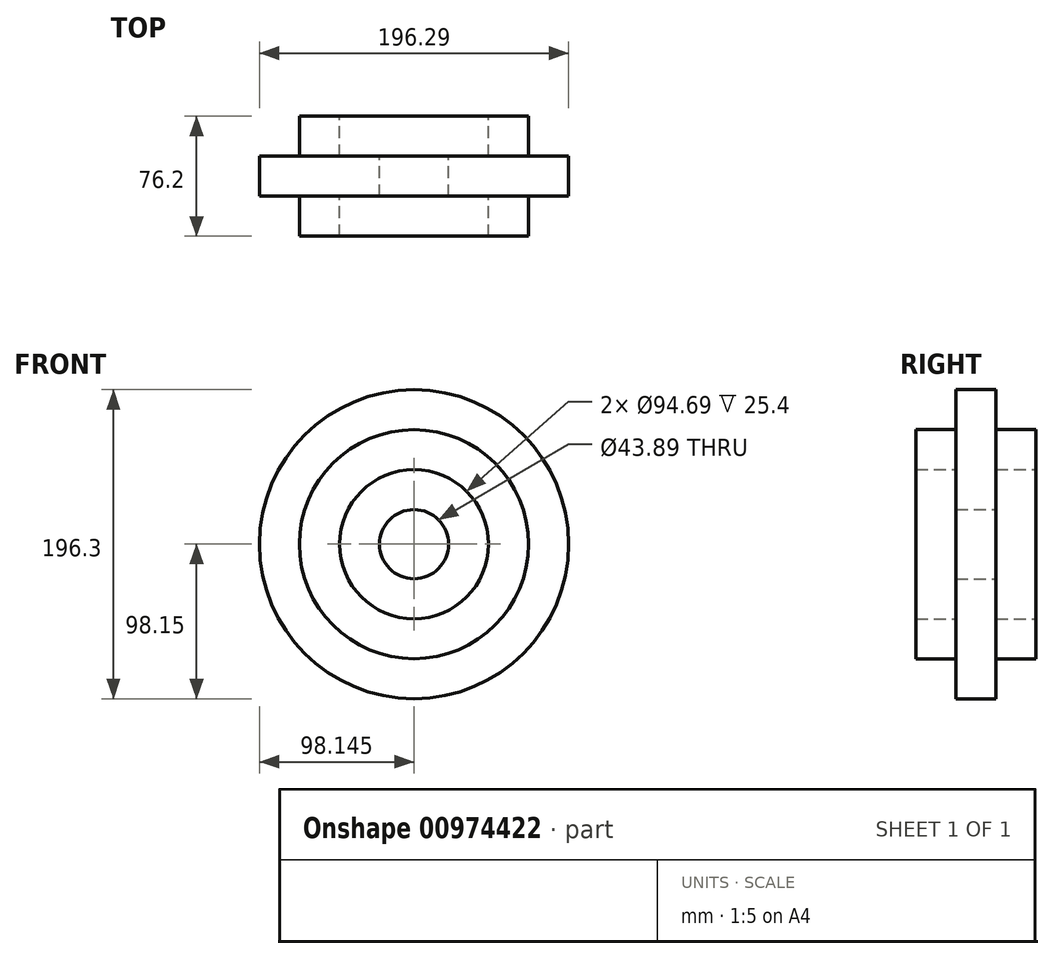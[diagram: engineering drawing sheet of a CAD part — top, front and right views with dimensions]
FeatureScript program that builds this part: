
annotation { "Feature Type Name" : "Feature", "Feature Type Description" : "" }
export const myFeature = defineFeature(function(context is Context, id is Id, definition is map)
    precondition{}
    {
        {
            var Q0;
            Q0=qCreatedBy(makeId("Top.planeOp"),FACE);
            var sketch = newSketch(context, id + "F0", { "sketchPlane" : qUnion([Q0])});
            skLineSegment(sketch, "E0", {"start": v(-40.21, -17.18) * mm, "end": v(-40.21, 8.22) * mm});
            skLineSegment(sketch, "E1", {"start": v(-40.21, 8.22) * mm, "end": v(-14.81, 8.22) * mm});
            skLineSegment(sketch, "E2", {"start": v(-14.81, 8.22) * mm, "end": v(-14.81, -17.18) * mm});
            skLineSegment(sketch, "E3", {"start": v(-14.81, -17.18) * mm, "end": v(10.59, -17.18) * mm});
            skLineSegment(sketch, "E4", {"start": v(10.59, -17.18) * mm, "end": v(10.59, -42.58) * mm});
            skLineSegment(sketch, "E5", {"start": v(10.59, -42.58) * mm, "end": v(-14.81, -42.58) * mm});
            skLineSegment(sketch, "E6", {"start": v(-14.81, -42.58) * mm, "end": v(-14.81, -67.98) * mm});
            skLineSegment(sketch, "E7", {"start": v(-14.81, -67.98) * mm, "end": v(-40.21, -67.98) * mm});
            skLineSegment(sketch, "E8", {"start": v(-40.21, -67.98) * mm, "end": v(-40.21, -42.58) * mm});
            skLineSegment(sketch, "E9", {"start": v(-40.21, -42.58) * mm, "end": v(-65.61, -42.58) * mm});
            skLineSegment(sketch, "E10", {"start": v(-65.61, -42.58) * mm, "end": v(-65.61, -17.18) * mm});
            skLineSegment(sketch, "E11", {"start": v(-65.61, -17.18) * mm, "end": v(-40.21, -17.18) * mm});
            skLineSegment(sketch, "E12", {"start": v(32.54, 10.94) * mm, "end": v(32.54, -75.79) * mm, "construction": true});
            skSolve(sketch);
        }
        {
            var Q0;
            Q0=makeQuery(id+"F0.imprint","IMPRINT",FACE,{"disambiguationData":[TD([[makeQuery(id+"F0.imprint","IMPRINT",EDGE,{"derivedFrom":sQuery(id+"F0.wireOp",EDGE,"E0")}),-1.0]])]});
            var Q1;
            Q1=sQuery(id+"F0.wireOp",EDGE,"E12");
            revolve(context, id + "F1", {"surfaceOperationType" : NewSurfaceOperationType.NEW, "entities" : qUnion([Q0]), "axis" : qUnion([Q1]), "revolveType" : RevolveType.FULL});
        }
    });
